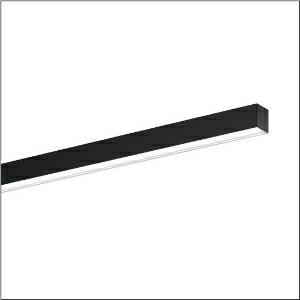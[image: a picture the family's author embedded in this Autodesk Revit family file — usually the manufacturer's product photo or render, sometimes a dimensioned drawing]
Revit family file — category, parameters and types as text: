
# Revit family: silica_r__21_51mx23db45bb_2d31
name_source: partatom
category: Lighting Fixtures
units: mm (PartAtom-declared; Revit-internal decimal feet)

## family parameters
Cut with Voids When Loaded = No
Host = Face
Light Source = No
Part Type = Normal
Room Calculation Point = No
Round Connector Dimension = Use Diameter
Shared = No

## types (1)
- --- (1 x LED, 4100 lm, 28.1 W, 4000K)
    Apparent Load = 28 VA
    CIE Flux Codes = 78 96 99 100 100
    Color Rendering = 80
    Color Temperature = 4000K
    Default Elevation = 1800 mm
    Description = Silica® 21, office luminaire, primary optical cover: prismatic diffuser, of PMMA, CAT 2 (L<= 3000cd/m²), light emission: direct distribution, primary light characteristic: symmetric, installation type: surface-mounted, LED, rated luminous flux: 4.100lm, luminous efficacy: 146lm/W, light colour: 840, colour temperature: 4000K, control gear: DALI 2, with terminal, 3+2-pole, max. 2.5mm², mains connection: 220..240V, AC, 50/60Hz, rated input power: 28.1W, luminaire housing, of aluminium, matt jet black (RAL 9005), length: 1.504mm, width: 53mm, height: 53mm, protection rating (complete): IP20, insulation class (complete): insulation class I (protective earthing), certification: CE, permissible operating ambient temperature: 0..+35°C, standard: EN 50419, packaging unit: 1 piece
    Height = 53 mm
    Lamp = 1 x LED
    Lamp Light Flux = 4100 lm
    Lamp Power = 28.1 W
    Lamp count = 1
    Length = 1504 mm
    Luminous efficacy = 146 lm/W
    Manufacturer = Siteco
    ModVariant = No
    Model = 51MX23DB45BB
    Mounting Place = Ceiling
    Mounting Type = Surface mounted
    Number of Poles = 1
    OnlyDefault = Yes
    Power Factor = 1
    Product Name = Silica® 21
    Product group = office luminaire | ceiling mounted
    ProductGroupID = 302
    Protection Class = Protection class I
    Protection Degree = IP 20
    RLX_Detail_Level = 1
    RLX_Emergency_Light_Flux = 0 lm
    RLX_Emergency_Type = 0
    RLX_Emergency_Type_DB = No
    RlxData = <blob elided: 23777 chars, md5=9b9023e6>
    Socket = socket
    Standby Power = 0 W
    System Light Flux = 4100 lm
    System Power = 28 W
    Type Comments = factory setting: luminous flux: 100 % | dim-lin: 254 | 323 mA
    Type Image = l_1335925.jpg
    URL = http://relux.com
    VarID = @adj_119422
    Voltage = 0 V
    Weight = 0.00 kg
    Width = 53 mm

## geometry (parser evidence)
native form markers: Blend x4, Sweep x10
no freeform markers — native parametric forms only
